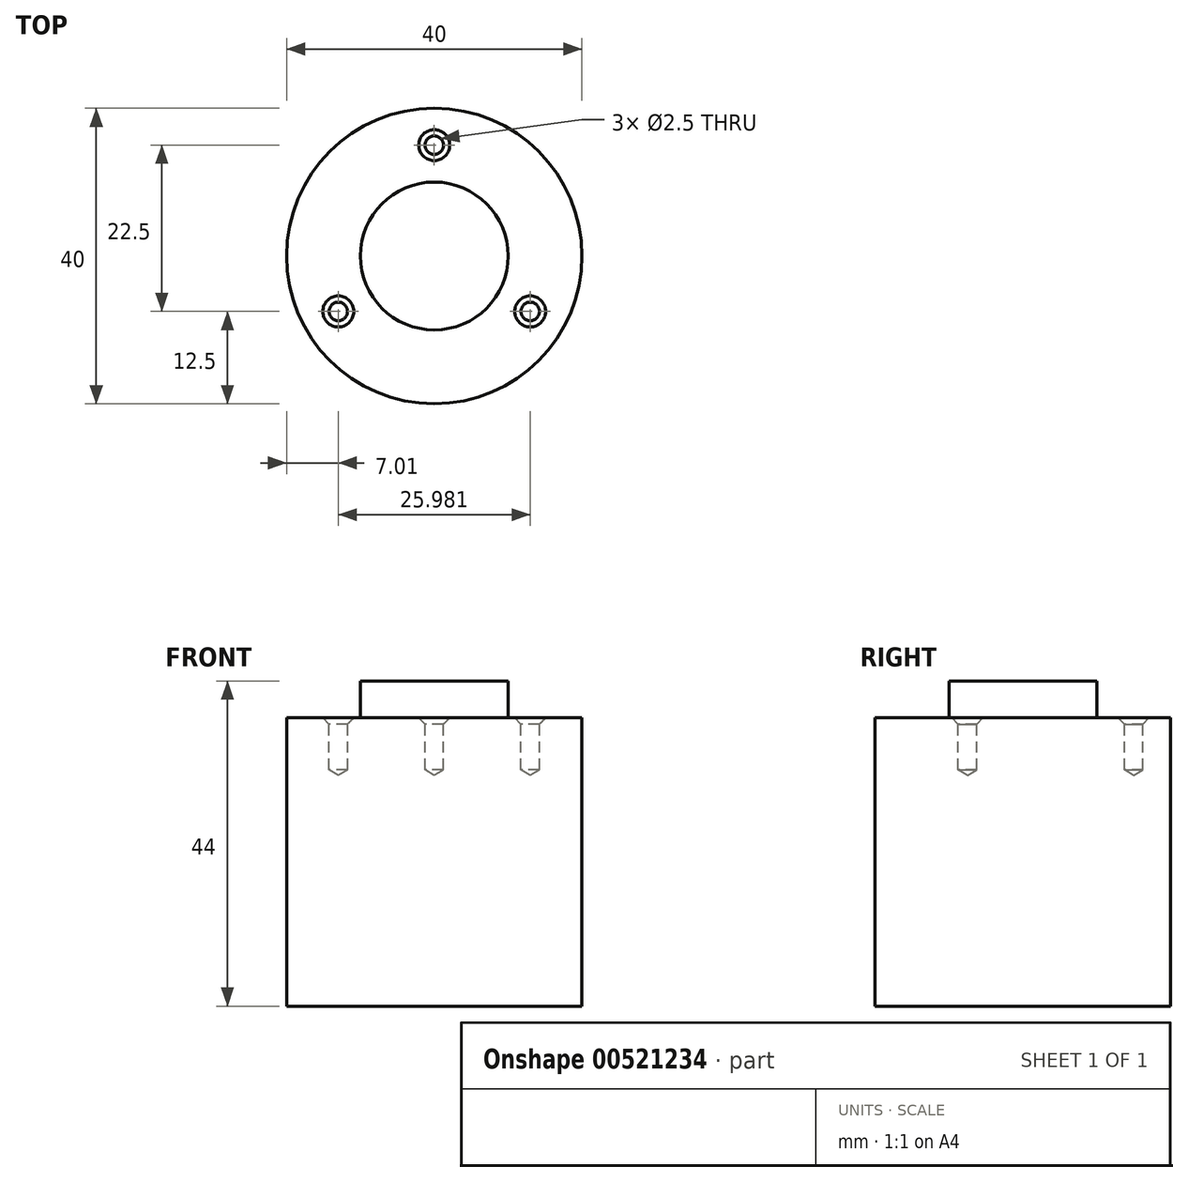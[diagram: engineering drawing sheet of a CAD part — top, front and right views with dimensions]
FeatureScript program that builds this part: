
annotation { "Feature Type Name" : "Feature", "Feature Type Description" : "" }
export const myFeature = defineFeature(function(context is Context, id is Id, definition is map)
    precondition{}
    {
        {
            var Q0;
            Q0=qCreatedBy(makeId("Top.planeOp"),FACE);
            var sketch = newSketch(context, id + "F0", { "sketchPlane" : qUnion([Q0])});
            skCircle(sketch, "E0", {"center": v(0, 0) * mm, "radius": 20 * mm});
            skSolve(sketch);
        }
        {
            var Q0;
            Q0=makeQuery(id+"F0.imprint","IMPRINT",FACE,{"disambiguationData":[TD([[makeQuery(id+"F0.imprint","IMPRINT",EDGE,{"derivedFrom":sQuery(id+"F0.wireOp",EDGE,"E0")}),1.0]])]});
            extrude(context, id + "F1", {"entities" : qUnion([Q0]), "depth" : 39 * mm, "offsetDistance" : 25.4 * mm});
        }
        {
            var Q0;
            Q0=makeQuery(id+"F1.opExtrude","CAP_FACE",FACE,{"disambiguationData":[OSD([sQuery(id+"F0.wireOp",EDGE,"E0")])],"isStart":false});
            var sketch = newSketch(context, id + "F2", { "sketchPlane" : qUnion([Q0])});
            skCircle(sketch, "E1", {"center": v(0, 0) * mm, "radius": 10 * mm});
            skSolve(sketch);
        }
        {
            var Q0;
            Q0 = qSketchRegion(id + "F2", true);
            extrude(context, id + "F3", {"entities" : qUnion([Q0]), "operationType" : NewBodyOperationType.ADD, "depth" : 5 * mm, "offsetDistance" : 25.4 * mm});
        }
        {
            var Q0;
            Q0=makeQuery(id+"F1.opExtrude","CAP_FACE",FACE,{"disambiguationData":[OSD([sQuery(id+"F0.wireOp",EDGE,"E0")])],"isStart":false});
            var sketch = newSketch(context, id + "F4", { "sketchPlane" : qUnion([Q0])});
            skPoint(sketch, "E2", {"position": v(0, 15) * mm});
            skPoint(sketch, "E3", {"position": v(13, -7.5) * mm});
            skPoint(sketch, "E4", {"position": v(-13, -7.5) * mm});
            skSolve(sketch);
        }
        {
            var Q0;
            Q0=sQuery(id+"F4.wireOp",VERTEX,"E4");
            var Q1;
            Q1=sQuery(id+"F4.wireOp",VERTEX,"E3");
            var Q2;
            Q2=sQuery(id+"F4.wireOp",VERTEX,"E2");
            var Q3;
            Q3=makeQuery(id+"F1.opExtrude","SWEPT_BODY",BODY,{"disambiguationData":[OSD([sQuery(id+"F0.wireOp",EDGE,"E0")])]});
            hole(context, id + "F5", {"style" : HoleStyle.C_SINK, "endStyle" : HoleEndStyle.BLIND, "holeDiameter" : 2.5 * mm, "cSinkDiameter" : 4.2 * mm, "cSinkAngle" : 90 * degree, "holeDepth" : 7 * mm, "isTappedThrough" : true, "tappedDepth" : 5.5 * mm, "tapClearance" : 3, "locations" : qUnion([Q0, Q1, Q2]), "scope" : qUnion([Q3])});
        }
    });
